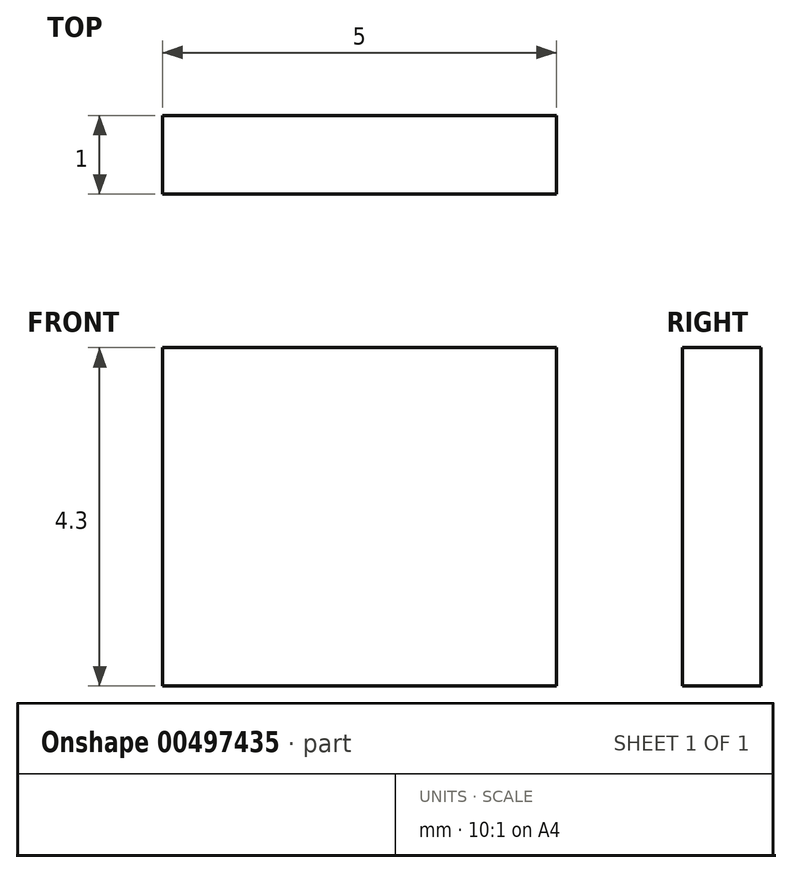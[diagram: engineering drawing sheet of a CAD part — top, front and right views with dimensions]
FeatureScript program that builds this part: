
annotation { "Feature Type Name" : "Feature", "Feature Type Description" : "" }
export const myFeature = defineFeature(function(context is Context, id is Id, definition is map)
    precondition{}
    {
        {
            var Q0;
            Q0=qCreatedBy(makeId("Front.planeOp"),FACE);
            var sketch = newSketch(context, id + "F0", { "sketchPlane" : qUnion([Q0])});
            skLineSegment(sketch, "E0.bottom", {"start": v(0, 0) * mm, "end": v(5, 0) * mm});
            skLineSegment(sketch, "E0.top", {"start": v(0, 4.3) * mm, "end": v(5, 4.3) * mm});
            skLineSegment(sketch, "E0.left", {"start": v(0, 0) * mm, "end": v(0, 4.3) * mm});
            skLineSegment(sketch, "E0.right", {"start": v(5, 0) * mm, "end": v(5, 4.3) * mm});
            skSolve(sketch);
        }
        {
            var Q0;
            Q0 = qSketchRegion(id + "F0", true);
            extrude(context, id + "F1", {"entities" : qUnion([Q0]), "depth" : 1 * mm});
        }
    });
